# Revit family: Operable-Walls_Modernfold_Encore_Single-Panles_Expandable-9_-Remote-Panel-Parallel-Stack
name_source: partatom
category: Specialty Equipment
units: mm (PartAtom-declared; Revit-internal decimal feet)

## family parameters
Always vertical = Yes
Classification Number = 23.25.40.17.14
Cut with Voids When Loaded = No
Enable Cutting in Views = No
Maintain Annotation Orientation = No
Part Type = Normal
Room Calculation Point = No
Round Connector Dimension = Use Diameter
Shared = No
Work Plane-Based = No

## types (1)
- Pocket Door Type I
    Bottom Seal Height = 0' - 2"
    Default Elevation = 0' - 0"
    Description = Encore - Expandable (9") Remote Panels - Single Panels - Parallel Stack - Pocket Door Type I
    Manufacturer = Modernfold
    Model = Acousti-Seal® Legacy® & Premier®
    Panel Material = Wall Finish - Modernfold - Grey
    Panel Thickness = 0' - 4 1/2"
    Seal Width = 0' - 1 1/2"
    Track Material = Track Color - Modernfold - White
    Track Trim = 0' - 0"
    Trim Material = Trim Color - Modernfold-Sherwin Williams® - Natural Choice
    URL = https://www.modernfold.com
    zClearanceHeight = 0' - 5"
    zNoPckt = Yes

## geometry (parser evidence)
native form markers: Sweep x19
no freeform markers — native parametric forms only
